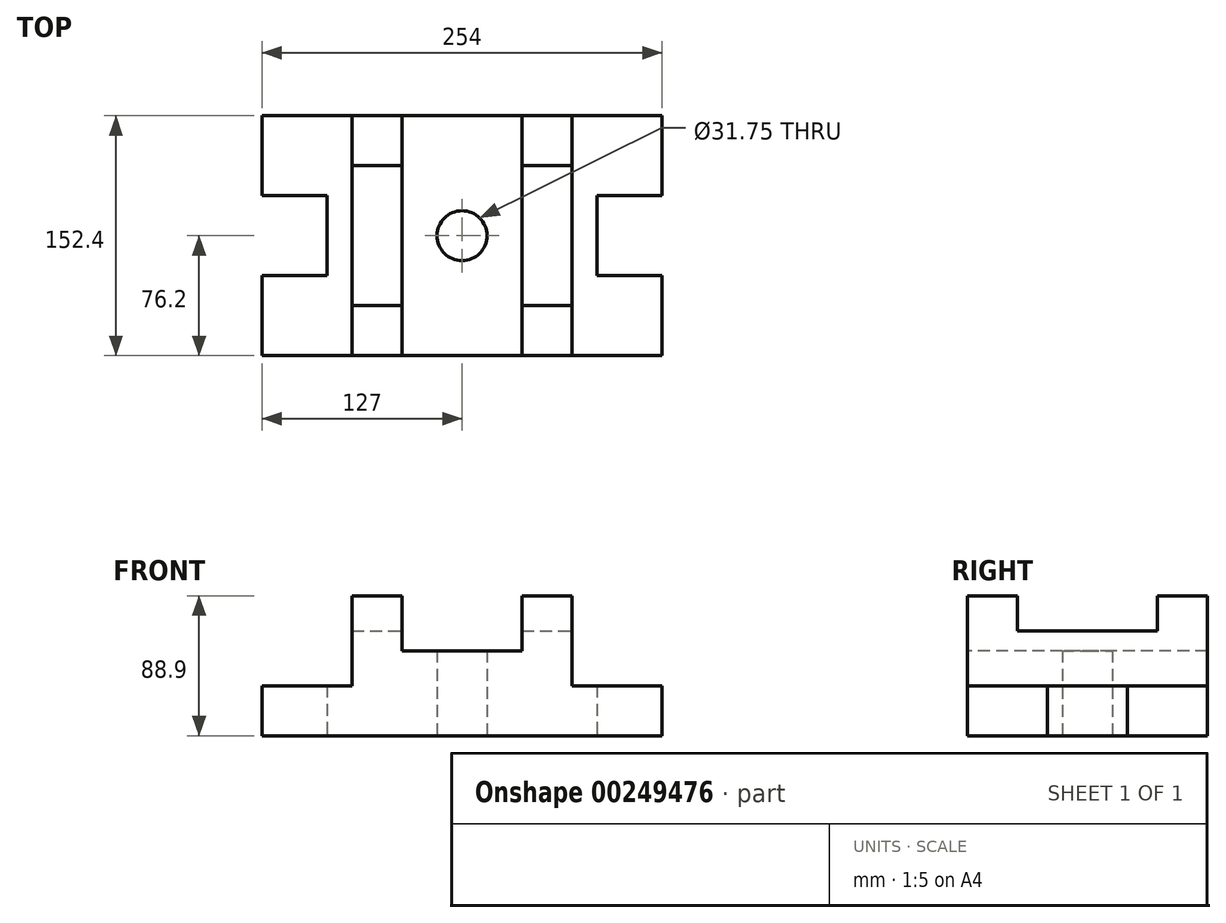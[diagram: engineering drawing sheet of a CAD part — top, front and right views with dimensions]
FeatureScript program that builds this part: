
annotation { "Feature Type Name" : "Feature", "Feature Type Description" : "" }
export const myFeature = defineFeature(function(context is Context, id is Id, definition is map)
    precondition{}
    {
        {
            var Q0;
            Q0=qCreatedBy(makeId("Top.planeOp"),FACE);
            var sketch = newSketch(context, id + "F0", { "sketchPlane" : qUnion([Q0])});
            skLineSegment(sketch, "E0.bottom", {"start": v(127, -76.2) * mm, "end": v(-127, -76.2) * mm});
            skLineSegment(sketch, "E0.top", {"start": v(127, 76.2) * mm, "end": v(-127, 76.2) * mm});
            skLineSegment(sketch, "E0.left", {"start": v(127, -76.2) * mm, "end": v(127, -25.4) * mm});
            skLineSegment(sketch, "E0.right", {"start": v(-127, -76.2) * mm, "end": v(-127, -25.4) * mm});
            skPoint(sketch, "E0.middle", {"position": v(0, 0) * mm});
            skLineSegment(sketch, "E1", {"start": v(-127, 25.4) * mm, "end": v(-85.72, 25.4) * mm});
            skLineSegment(sketch, "E2", {"start": v(-85.72, -25.4) * mm, "end": v(-127, -25.4) * mm});
            skLineSegment(sketch, "E3", {"start": v(-127, -25.4) * mm, "end": v(-85.72, -25.4) * mm});
            skLineSegment(sketch, "E4", {"start": v(-85.72, 25.4) * mm, "end": v(-85.72, -25.4) * mm});
            skLineSegment(sketch, "E5", {"start": v(127, 25.4) * mm, "end": v(85.72, 25.4) * mm});
            skLineSegment(sketch, "E6", {"start": v(85.72, 25.4) * mm, "end": v(85.72, -25.4) * mm});
            skLineSegment(sketch, "E7", {"start": v(85.72, -25.4) * mm, "end": v(127, -25.4) * mm});
            skLineSegment(sketch, "E8", {"start": v(-69.85, 76.2) * mm, "end": v(-69.85, -76.2) * mm});
            skLineSegment(sketch, "E9", {"start": v(-38.1, 76.2) * mm, "end": v(-38.1, -76.2) * mm});
            skLineSegment(sketch, "E10", {"start": v(69.85, 76.2) * mm, "end": v(69.85, -76.2) * mm});
            skLineSegment(sketch, "E11", {"start": v(38.1, -76.2) * mm, "end": v(38.1, 76.2) * mm});
            skLineSegment(sketch, "E12", {"start": v(-69.85, 44.45) * mm, "end": v(-38.1, 44.45) * mm});
            skLineSegment(sketch, "E13", {"start": v(-69.85, -44.45) * mm, "end": v(-38.1, -44.45) * mm});
            skLineSegment(sketch, "E14.trimOffspring", {"start": v(38.1, 44.45) * mm, "end": v(69.85, 44.45) * mm});
            skLineSegment(sketch, "E15.trimOffspring", {"start": v(38.1, -44.45) * mm, "end": v(69.85, -44.45) * mm});
            skCircle(sketch, "E16", {"center": v(0, 0) * mm, "radius": 15.88 * mm});
            skLineSegment(sketch, "E17.trimOffspring", {"start": v(-127, 25.4) * mm, "end": v(-127, 76.2) * mm});
            skLineSegment(sketch, "E18.trimOffspring", {"start": v(127, 25.4) * mm, "end": v(127, 76.2) * mm});
            skSolve(sketch);
        }
        {
            var Q0;
            {var subQ5=sQuery(id+"F0.wireOp",EDGE,"E15.trimOffspring");Q0=makeQuery(id+"F0.imprint","IMPRINT",FACE,{"disambiguationData":[TD([[makeQuery(id+"F0.imprint","IMPRINT",EDGE,{"derivedFrom":subQ5}),-1.0]])]});}
            var Q1;
            {var subQ5=sQuery(id+"F0.wireOp",EDGE,"E13");Q1=makeQuery(id+"F0.imprint","IMPRINT",FACE,{"disambiguationData":[TD([[makeQuery(id+"F0.imprint","IMPRINT",EDGE,{"derivedFrom":subQ5}),-1.0]])]});}
            var Q2;
            {var subQ5=sQuery(id+"F0.wireOp",EDGE,"E14.trimOffspring");Q2=makeQuery(id+"F0.imprint","IMPRINT",FACE,{"disambiguationData":[TD([[makeQuery(id+"F0.imprint","IMPRINT",EDGE,{"derivedFrom":subQ5}),1.0]])]});}
            var Q3;
            {var subQ5=sQuery(id+"F0.wireOp",EDGE,"E12");Q3=makeQuery(id+"F0.imprint","IMPRINT",FACE,{"disambiguationData":[TD([[makeQuery(id+"F0.imprint","IMPRINT",EDGE,{"derivedFrom":subQ5}),1.0]])]});}
            var Q4;
            {var subQ3=sQuery(id+"F0.wireOp",EDGE,"E5");Q4=makeQuery(id+"F0.imprint","IMPRINT",FACE,{"disambiguationData":[TD([[makeQuery(id+"F0.imprint","IMPRINT",EDGE,{"derivedFrom":subQ3}),-1.0]])]});}
            var Q5;
            {var subQ3=sQuery(id+"F0.wireOp",EDGE,"E1");Q5=makeQuery(id+"F0.imprint","IMPRINT",FACE,{"disambiguationData":[TD([[makeQuery(id+"F0.imprint","IMPRINT",EDGE,{"derivedFrom":subQ3}),1.0]])]});}
            var Q6;
            {var subQ0=sQuery(id+"F0.wireOp",EDGE,"E9");var subQ7=sQuery(id+"F0.wireOp",EDGE,"E0.bottom");var subQ8=makeQuery(id+"F0.imprint","INTERSECT",VERTEX,{"derivedFrom":[subQ7,subQ0]});Q6=makeQuery(id+"F0.imprint","IMPRINT",FACE,{"disambiguationData":[TD([[makeQuery(id+"F0.imprint","IMPRINT",EDGE,{"disambiguationData":[TD([[subQ8,1.0]])],"derivedFrom":subQ7}),-1.0]])]});}
            var Q7;
            {var subQ0=sQuery(id+"F0.wireOp",EDGE,"E12");Q7=makeQuery(id+"F0.imprint","IMPRINT",FACE,{"disambiguationData":[TD([[makeQuery(id+"F0.imprint","IMPRINT",EDGE,{"derivedFrom":subQ0}),-1.0]])]});}
            var Q8;
            {var subQ0=sQuery(id+"F0.wireOp",EDGE,"E14.trimOffspring");Q8=makeQuery(id+"F0.imprint","IMPRINT",FACE,{"disambiguationData":[TD([[makeQuery(id+"F0.imprint","IMPRINT",EDGE,{"derivedFrom":subQ0}),-1.0]])]});}
            extrude(context, id + "F1", {"entities" : qUnion([Q0, Q1, Q2, Q3, Q4, Q5, Q6, Q7, Q8]), "depth" : 31.75 * mm});
        }
        {
            var Q0;
            Q0=makeQuery(id+"F0.imprint","IMPRINT",FACE,{"disambiguationData":[TD([[makeQuery(id+"F0.imprint","IMPRINT",EDGE,{"derivedFrom":sQuery(id+"F0.wireOp",EDGE,"E16")}),-1.0]])]});
            extrude(context, id + "F2", {"entities" : qUnion([Q0]), "operationType" : NewBodyOperationType.ADD, "depth" : 53.97 * mm});
        }
        {
            var Q0;
            {var subQ0=sQuery(id+"F0.wireOp",EDGE,"E12");Q0=makeQuery(id+"F0.imprint","IMPRINT",FACE,{"disambiguationData":[TD([[makeQuery(id+"F0.imprint","IMPRINT",EDGE,{"derivedFrom":subQ0}),-1.0]])]});}
            var Q1;
            {var subQ0=sQuery(id+"F0.wireOp",EDGE,"E14.trimOffspring");Q1=makeQuery(id+"F0.imprint","IMPRINT",FACE,{"disambiguationData":[TD([[makeQuery(id+"F0.imprint","IMPRINT",EDGE,{"derivedFrom":subQ0}),-1.0]])]});}
            extrude(context, id + "F3", {"entities" : qUnion([Q0, Q1]), "operationType" : NewBodyOperationType.ADD, "depth" : 66.67 * mm});
        }
        {
            var Q0;
            {var subQ5=sQuery(id+"F0.wireOp",EDGE,"E12");Q0=makeQuery(id+"F0.imprint","IMPRINT",FACE,{"disambiguationData":[TD([[makeQuery(id+"F0.imprint","IMPRINT",EDGE,{"derivedFrom":subQ5}),1.0]])]});}
            var Q1;
            {var subQ5=sQuery(id+"F0.wireOp",EDGE,"E14.trimOffspring");Q1=makeQuery(id+"F0.imprint","IMPRINT",FACE,{"disambiguationData":[TD([[makeQuery(id+"F0.imprint","IMPRINT",EDGE,{"derivedFrom":subQ5}),1.0]])]});}
            var Q2;
            {var subQ5=sQuery(id+"F0.wireOp",EDGE,"E13");Q2=makeQuery(id+"F0.imprint","IMPRINT",FACE,{"disambiguationData":[TD([[makeQuery(id+"F0.imprint","IMPRINT",EDGE,{"derivedFrom":subQ5}),-1.0]])]});}
            var Q3;
            {var subQ5=sQuery(id+"F0.wireOp",EDGE,"E15.trimOffspring");Q3=makeQuery(id+"F0.imprint","IMPRINT",FACE,{"disambiguationData":[TD([[makeQuery(id+"F0.imprint","IMPRINT",EDGE,{"derivedFrom":subQ5}),-1.0]])]});}
            extrude(context, id + "F4", {"entities" : qUnion([Q0, Q1, Q2, Q3]), "operationType" : NewBodyOperationType.ADD, "depth" : 88.9 * mm});
        }
    });
